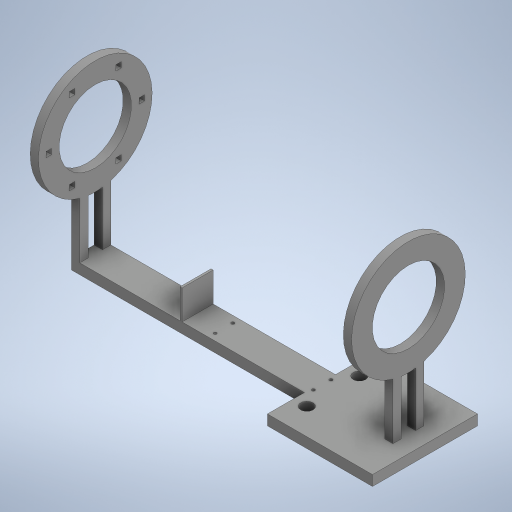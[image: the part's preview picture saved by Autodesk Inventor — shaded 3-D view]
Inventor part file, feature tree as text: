
AUTODESK INVENTOR PART (.ipt)
format: ipt  version: 2023 (Build 270158000, 158)  size: 554,496 bytes
history: native  units: in
note: dims shown in document units (in); Inventor stores cm internally (conversion verified against a paired STEP export)
features: extrude x9, sketch x4, projected_geometry x2, pattern_linear x1
ambient origin geometry x8: Origin, YZ Plane, XZ Plane, XY Plane, X Axis, Y Axis, Z Axis, Center Point
bodies: Solid1 (feature_tree)
feature tree (16):
  extrude  "Extrusion1"  Depth=0.2047in
  extrude  "Extrusion2"  Depth=0.2047in TaperAngle=360.0deg
  extrude  "Extrusion3"  Depth=0.315in
  sketch  "Sketch2"  dims[d8=1.378in d9=1.7717in d10=0.9843in d11=0.8189in d12=1.1811in d13=0.315in d14=0.315in d15=360.0deg d16=0.1575in d17=0.1575in d18=360.0deg d22=1.1811in d23=0.315in d24=1.1811in d25=1.378in d26=1.378in d27=0.1575in d30=0.2047in]
  extrude  "Extrusion4"  Depth=0.2047in
  extrude  "Extrusion5"  Depth=0.2047in
  pattern_linear  "Rectangular Pattern1"  Spacing1=0.315in  [1 undecoded]
  extrude  "Extrusion7"  Depth=0.315in
  extrude  "Extrusion8"  Depth=0.2047in
  extrude  "Extrusion9"  Depth=0.2047in
  extrude  "Extrusion6"  Depth=0.8465in
  sketch  "Sketch3"  dims[d31=0.2047in d32=2.3622in d34=360.0deg]
  projected_geometry  "Projected Loop1"
  sketch  "Sketch4"  dims[d36=0.315in d37=0.315in d38=0.2047in d39=0.2047in d40=0.315in d41=0.315in d42=0.2047in d43=0.2047in d44=0.8465in d45=4.3307in d46=2.7559in d47=0.5906in d49=0.315in d50=1.122in d51=0.3937in d52=0.315in d53=0.0in d54=0.315in d55=0.0in d56=12.874in d57=0.0in d58=4.0in d59=4.0in d60=0.4724in d63=0.2559in d65=3.8976in d66=1.0039in d67=0.3346in d68=0.1181in d69=0.7874in d71=3.7402in d72=0.3937in d74=0.3937in d76=0.3937in d77=0.0in d78=0.3937in d79=0.0in d80=1.0in d81=0.5in d82=3.0118in d83=0.3937in d84=0.0in d85=0.7874in d87=11.9291in d88=0.122in d89=0.0in d90=0.122in d91=0.0in d92=0.0787in d93=1.5157in d94=0.0in]
  projected_geometry  "Projected Loop2"
  sketch  "Sketch1"  dims[d1=2.3622in d3=2.3622in]
note: 1 required parameter value undecoded (feature->parameter linkage not recoverable at this tier; creation-order binding heuristic only, values carry confidence <= 0.55)
